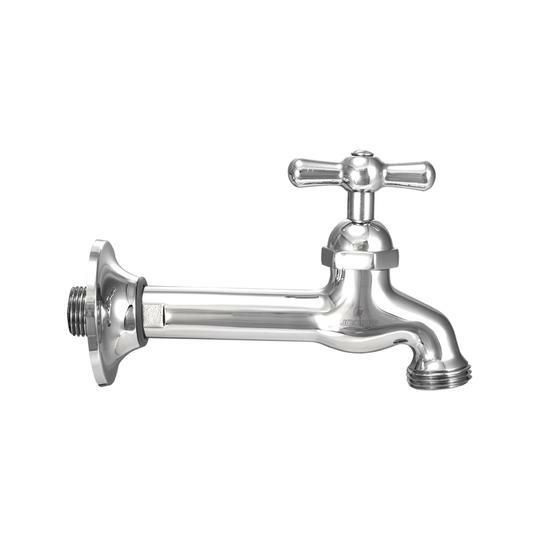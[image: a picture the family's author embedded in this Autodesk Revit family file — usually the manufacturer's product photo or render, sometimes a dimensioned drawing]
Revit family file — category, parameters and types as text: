
# Revit family: 01-9954-11 LLAVE EXTENSION MANGUERA METAL CROMO
name_source: partatom
category: Plumbing Fixtures
revit_build: Autodesk Revit 2018 (Build: 20170223_1515(x64)
units: mm (PartAtom-declared; Revit-internal decimal feet)

## family parameters
Cut with Voids When Loaded = No
Host = Face
OmniClass Number = 23.31.11.00
Part Type = Normal
Room Calculation Point = No
Round Connector Dimension = Use Diameter
Shared = No

## types (1)
- 01-9954-11
    Acometida = Dim 1/2" NPT
    Alto = 90 mm  [stored 0.295276 ft]
    Ancho = 163 mm
    Ancho manija llave = 60 mm  [stored 0.19685 ft]
    CW Connection = Yes
    Default Elevation = 0 mm  [stored 0 ft]
    Description = Llave jardin
    Dim Escudo = 60 mm  [stored 0.19685 ft]
    HW Connection = Yes
    Link Ficha Tecnica = http://infotecnica.gricol.com
    Manufacturer = Gricol
    Metal laton cromado = Metal Laton Cromado
    Model = 01-9954-11
    Product Name = LLAVE EXTENSION MANGUERA METAL CROMO
    Salida = Dim 3/4" NH
    Type Image = LLAVE EXTENSION MANGUERA METAL CROMO.JPG
    URL = https://www.gricol.com
    Vent Connection = No
    Waste Connection = No

note: [stored X ft] marks values corroborated as IEEE doubles in the binary element streams (Revit-internal decimal feet)

## geometry (parser evidence)
native form markers: Blend x2, Sweep x2
no freeform markers — native parametric forms only
